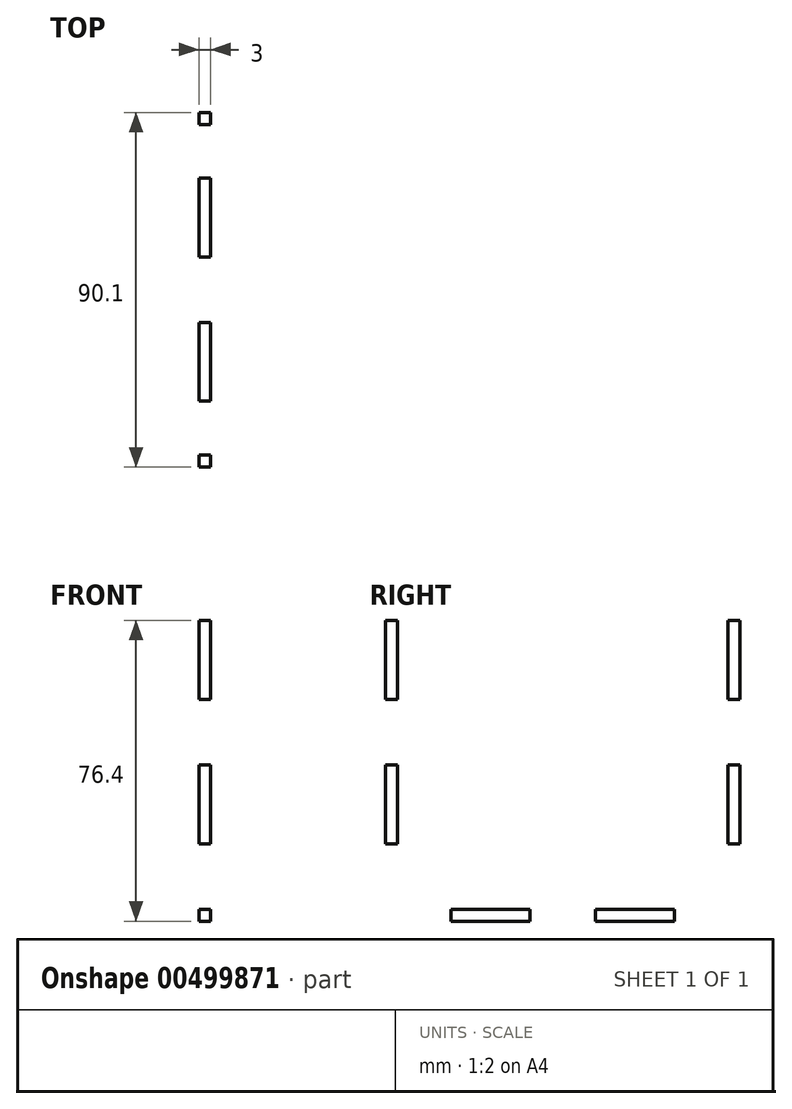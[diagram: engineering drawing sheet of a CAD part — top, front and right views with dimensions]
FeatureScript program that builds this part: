
annotation { "Feature Type Name" : "Feature", "Feature Type Description" : "" }
export const myFeature = defineFeature(function(context is Context, id is Id, definition is map)
    precondition{}
    {
        {
            var Q0;
            Q0=qCreatedBy(makeId("Right.planeOp"),FACE);
            var sketch = newSketch(context, id + "F0", { "sketchPlane" : qUnion([Q0])});
            skLineSegment(sketch, "E0.bottom", {"start": v(42, -45) * mm, "end": v(-42, -45) * mm});
            skLineSegment(sketch, "E0.top", {"start": v(42, 45) * mm, "end": v(-42, 45) * mm});
            skLineSegment(sketch, "E0.left", {"start": v(42, -45) * mm, "end": v(42, 45) * mm});
            skLineSegment(sketch, "E0.right", {"start": v(-42, -45) * mm, "end": v(-42, 45) * mm});
            skPoint(sketch, "E0.middle", {"position": v(0, 0) * mm});
            skLineSegment(sketch, "E1.bottom", {"start": v(-8.35, -48.05) * mm, "end": v(-28.35, -48.05) * mm});
            skLineSegment(sketch, "E1.top", {"start": v(-8.35, -45) * mm, "end": v(-28.35, -45) * mm});
            skLineSegment(sketch, "E1.left", {"start": v(-8.35, -48.05) * mm, "end": v(-8.35, -45) * mm});
            skLineSegment(sketch, "E1.right", {"start": v(-28.35, -48.05) * mm, "end": v(-28.35, -45) * mm});
            skPoint(sketch, "E1.middle", {"position": v(-18.35, -46.52) * mm});
            skLineSegment(sketch, "E2.bottom", {"start": v(28.35, -48.05) * mm, "end": v(8.35, -48.05) * mm});
            skLineSegment(sketch, "E2.top", {"start": v(28.35, -45) * mm, "end": v(8.35, -45) * mm});
            skLineSegment(sketch, "E2.left", {"start": v(28.35, -48.05) * mm, "end": v(28.35, -45) * mm});
            skLineSegment(sketch, "E2.right", {"start": v(8.35, -48.05) * mm, "end": v(8.35, -45) * mm});
            skPoint(sketch, "E2.middle", {"position": v(18.35, -46.52) * mm});
            skLineSegment(sketch, "E3.bottom", {"start": v(-42, 8.35) * mm, "end": v(-45.05, 8.35) * mm});
            skLineSegment(sketch, "E3.top", {"start": v(-42, 28.35) * mm, "end": v(-45.05, 28.35) * mm});
            skLineSegment(sketch, "E3.left", {"start": v(-42, 8.35) * mm, "end": v(-42, 28.35) * mm});
            skLineSegment(sketch, "E3.right", {"start": v(-45.05, 8.35) * mm, "end": v(-45.05, 28.35) * mm});
            skPoint(sketch, "E3.middle", {"position": v(-43.53, 18.35) * mm});
            skLineSegment(sketch, "E4.bottom", {"start": v(-42, -28.35) * mm, "end": v(-45.05, -28.35) * mm});
            skLineSegment(sketch, "E4.top", {"start": v(-42, -8.35) * mm, "end": v(-45.05, -8.35) * mm});
            skLineSegment(sketch, "E4.left", {"start": v(-42, -28.35) * mm, "end": v(-42, -8.35) * mm});
            skLineSegment(sketch, "E4.right", {"start": v(-45.05, -28.35) * mm, "end": v(-45.05, -8.35) * mm});
            skPoint(sketch, "E4.middle", {"position": v(-43.53, -18.35) * mm});
            skLineSegment(sketch, "E5.bottom", {"start": v(45.05, -28.35) * mm, "end": v(42, -28.35) * mm});
            skLineSegment(sketch, "E5.top", {"start": v(45.05, -8.35) * mm, "end": v(42, -8.35) * mm});
            skLineSegment(sketch, "E5.left", {"start": v(45.05, -28.35) * mm, "end": v(45.05, -8.35) * mm});
            skLineSegment(sketch, "E5.right", {"start": v(42, -28.35) * mm, "end": v(42, -8.35) * mm});
            skPoint(sketch, "E5.middle", {"position": v(43.53, -18.35) * mm});
            skLineSegment(sketch, "E6.bottom", {"start": v(45.05, 8.35) * mm, "end": v(42, 8.35) * mm});
            skLineSegment(sketch, "E6.top", {"start": v(45.05, 28.35) * mm, "end": v(42, 28.35) * mm});
            skLineSegment(sketch, "E6.left", {"start": v(45.05, 8.35) * mm, "end": v(45.05, 28.35) * mm});
            skLineSegment(sketch, "E6.right", {"start": v(42, 8.35) * mm, "end": v(42, 28.35) * mm});
            skPoint(sketch, "E6.middle", {"position": v(43.53, 18.35) * mm});
            skLineSegment(sketch, "E7.bottom", {"start": v(-5.35, 45) * mm, "end": v(-25.35, 45) * mm});
            skLineSegment(sketch, "E7.top", {"start": v(-5.35, 48.05) * mm, "end": v(-25.35, 48.05) * mm});
            skLineSegment(sketch, "E7.left", {"start": v(-5.35, 45) * mm, "end": v(-5.35, 48.05) * mm});
            skLineSegment(sketch, "E7.right", {"start": v(-25.35, 45) * mm, "end": v(-25.35, 48.05) * mm});
            skPoint(sketch, "E7.middle", {"position": v(-15.35, 46.52) * mm});
            skLineSegment(sketch, "E8.bottom", {"start": v(25.35, 45) * mm, "end": v(5.35, 45) * mm});
            skLineSegment(sketch, "E8.top", {"start": v(25.35, 48.05) * mm, "end": v(5.35, 48.05) * mm});
            skLineSegment(sketch, "E8.left", {"start": v(25.35, 45) * mm, "end": v(25.35, 48.05) * mm});
            skLineSegment(sketch, "E8.right", {"start": v(5.35, 45) * mm, "end": v(5.35, 48.05) * mm});
            skPoint(sketch, "E8.middle", {"position": v(15.35, 46.52) * mm});
            skSolve(sketch);
        }
        {
            var Q0;
            {var subQ14=sQuery(id+"F0.wireOp",EDGE,"E1.top");Q0=makeQuery(id+"F0.imprint","IMPRINT",FACE,{"disambiguationData":[TD([[makeQuery(id+"F0.imprint","IMPRINT",EDGE,{"derivedFrom":subQ14}),-1.0]])]});}
            var Q1;
            Q1=makeQuery(id+"F0.imprint","IMPRINT",FACE,{"disambiguationData":[TD([[makeQuery(id+"F0.imprint","IMPRINT",EDGE,{"derivedFrom":sQuery(id+"F0.wireOp",EDGE,"E3.bottom")}),-1.0]])]});
            var Q2;
            Q2=makeQuery(id+"F0.imprint","IMPRINT",FACE,{"disambiguationData":[TD([[makeQuery(id+"F0.imprint","IMPRINT",EDGE,{"derivedFrom":sQuery(id+"F0.wireOp",EDGE,"E4.bottom")}),-1.0]])]});
            var Q3;
            Q3=makeQuery(id+"F0.imprint","IMPRINT",FACE,{"disambiguationData":[TD([[makeQuery(id+"F0.imprint","IMPRINT",EDGE,{"derivedFrom":sQuery(id+"F0.wireOp",EDGE,"E1.bottom")}),-1.0]])]});
            var Q4;
            Q4=makeQuery(id+"F0.imprint","IMPRINT",FACE,{"disambiguationData":[TD([[makeQuery(id+"F0.imprint","IMPRINT",EDGE,{"derivedFrom":sQuery(id+"F0.wireOp",EDGE,"E2.bottom")}),-1.0]])]});
            var Q5;
            Q5=makeQuery(id+"F0.imprint","IMPRINT",FACE,{"disambiguationData":[TD([[makeQuery(id+"F0.imprint","IMPRINT",EDGE,{"derivedFrom":sQuery(id+"F0.wireOp",EDGE,"E5.bottom")}),-1.0]])]});
            var Q6;
            Q6=makeQuery(id+"F0.imprint","IMPRINT",FACE,{"disambiguationData":[TD([[makeQuery(id+"F0.imprint","IMPRINT",EDGE,{"derivedFrom":sQuery(id+"F0.wireOp",EDGE,"E6.bottom")}),-1.0]])]});
            var Q7;
            Q7=makeQuery(id+"F0.imprint","IMPRINT",FACE,{"disambiguationData":[TD([[makeQuery(id+"F0.imprint","IMPRINT",EDGE,{"derivedFrom":sQuery(id+"F0.wireOp",EDGE,"E8.bottom")}),-1.0]])]});
            var Q8;
            Q8=makeQuery(id+"F0.imprint","IMPRINT",FACE,{"disambiguationData":[TD([[makeQuery(id+"F0.imprint","IMPRINT",EDGE,{"derivedFrom":sQuery(id+"F0.wireOp",EDGE,"E7.bottom")}),-1.0]])]});
            extrude(context, id + "F1", {"entities" : qUnion([Q0, Q1, Q2, Q3, Q4, Q5, Q6, Q7, Q8]), "depth" : 3 * mm, "offsetDistance" : 25 * mm});
        }
    });
